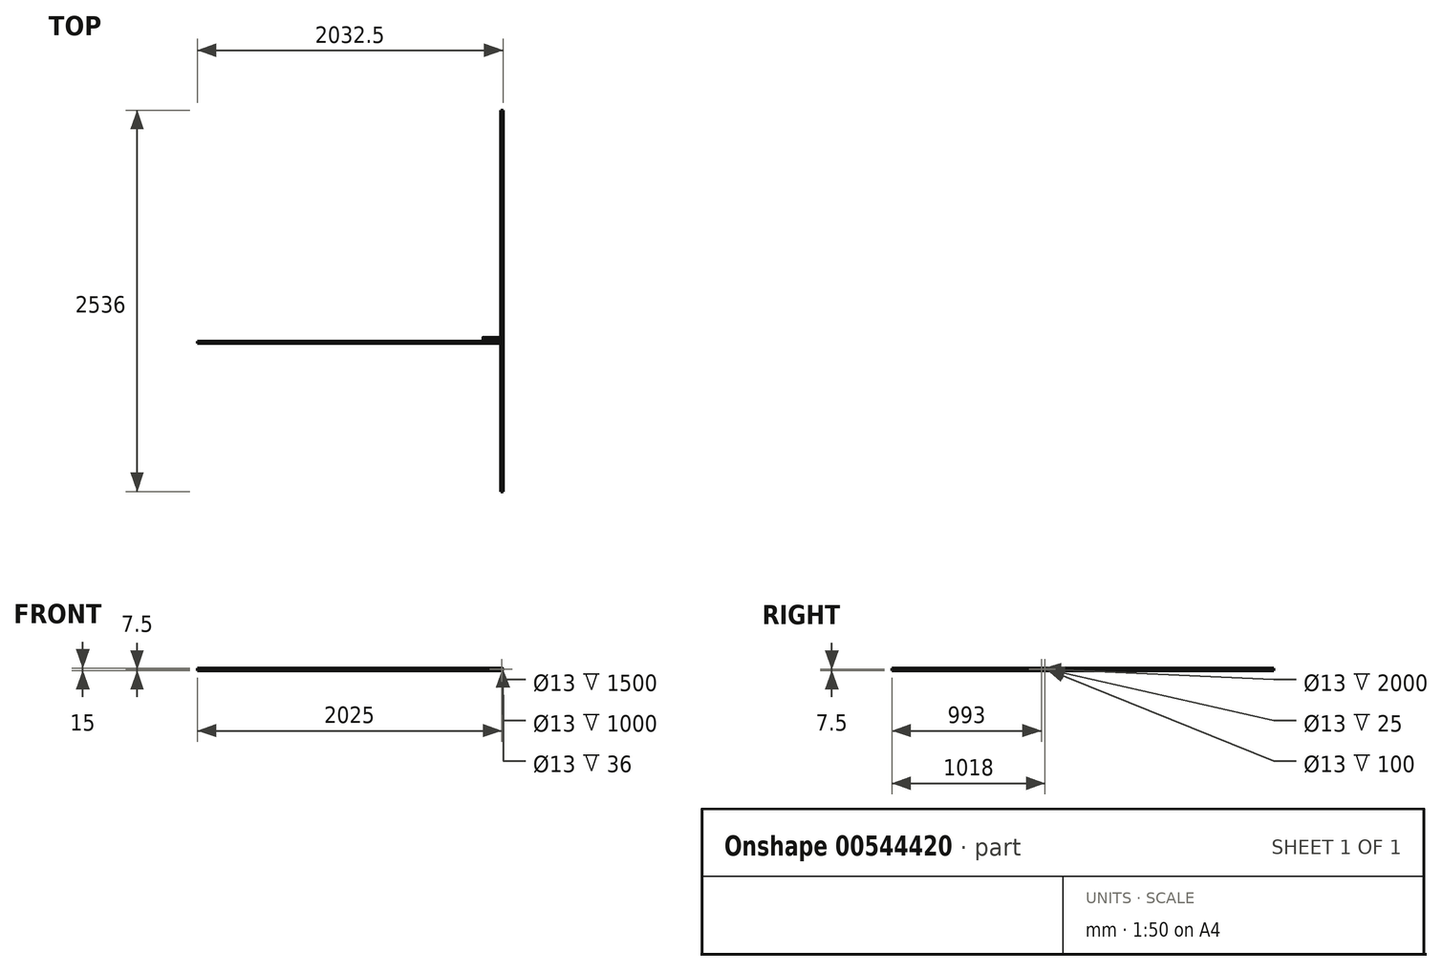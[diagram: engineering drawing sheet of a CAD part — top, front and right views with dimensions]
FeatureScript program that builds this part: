
annotation { "Feature Type Name" : "Feature", "Feature Type Description" : "" }
export const myFeature = defineFeature(function(context is Context, id is Id, definition is map)
    precondition{}
    {
        {
            var Q0;
            Q0=qCreatedBy(makeId("Front.planeOp"),FACE);
            var sketch = newSketch(context, id + "F0", { "sketchPlane" : qUnion([Q0])});
            skCircle(sketch, "E0", {"center": v(25, 0) * mm, "radius": 7.5 * mm});
            skCircle(sketch, "E1", {"center": v(25, 0) * mm, "radius": 6.5 * mm});
            skLineSegment(sketch, "E2", {"start": v(0, 0) * mm, "end": v(0, -17.9) * mm});
            skSolve(sketch);
        }
        {
            var Q0;
            Q0=makeQuery(id+"F0.imprint","IMPRINT",FACE,{"disambiguationData":[TD([[makeQuery(id+"F0.imprint","IMPRINT",EDGE,{"derivedFrom":sQuery(id+"F0.wireOp",EDGE,"E0")}),1.0]])]});
            extrude(context, id + "F1", {"entities" : qUnion([Q0]), "depth" : 18 * mm, "offsetDistance" : 25 * mm, "hasSecondDirection" : true, "secondDirectionOppositeDirection" : true, "secondDirectionDepth" : 18 * mm});
        }
        {
            var Q0;
            Q0=qCreatedBy(makeId("Right.planeOp"),FACE);
            var sketch = newSketch(context, id + "F2", { "sketchPlane" : qUnion([Q0])});
            skCircle(sketch, "E3", {"center": v(0, 0) * mm, "radius": 7.5 * mm});
            skCircle(sketch, "E4", {"center": v(0, 0) * mm, "radius": 6.5 * mm});
            skSolve(sketch);
        }
        {
            var Q0;
            Q0=makeQuery(id+"F2.imprint","IMPRINT",FACE,{"disambiguationData":[TD([[makeQuery(id+"F2.imprint","IMPRINT",EDGE,{"derivedFrom":sQuery(id+"F2.wireOp",EDGE,"E4")}),1.0]])]});
            var Q1;
            Q1=makeQuery(id+"F1.opExtrude","SWEPT_FACE",FACE,{"disambiguationData":[OSD([sQuery(id+"F0.wireOp",EDGE,"E1")])]});
            var Q2;
            Q2=makeQuery(id+"F1.opExtrude","SWEPT_BODY",BODY,{"disambiguationData":[OSD([sQuery(id+"F0.wireOp",EDGE,"E0"),sQuery(id+"F0.wireOp",EDGE,"E1")])]});
            extrude(context, id + "F3", {"entities" : qUnion([Q0]), "operationType" : NewBodyOperationType.REMOVE, "endBound" : BoundingType.UP_TO_SURFACE, "depth" : 25 * mm, "endBoundEntityFace" : qUnion([Q1]), "endBoundEntityBody" : qUnion([Q2]), "offsetDistance" : 25 * mm});
        }
        {
            var Q0;
            Q0=makeQuery(id+"F2.imprint","IMPRINT",FACE,{"disambiguationData":[TD([[makeQuery(id+"F2.imprint","IMPRINT",EDGE,{"derivedFrom":sQuery(id+"F2.wireOp",EDGE,"E3")}),1.0]])]});
            var Q1;
            Q1=makeQuery(id+"F1.opExtrude","SWEPT_BODY",BODY,{"disambiguationData":[OSD([sQuery(id+"F0.wireOp",EDGE,"E0"),sQuery(id+"F0.wireOp",EDGE,"E1")])]});
            extrude(context, id + "F4", {"entities" : qUnion([Q0]), "operationType" : NewBodyOperationType.ADD, "endBound" : BoundingType.UP_TO_BODY, "depth" : 25 * mm, "endBoundEntityBody" : qUnion([Q1]), "offsetDistance" : 25 * mm});
        }
        {
            var Q0;
            Q0=makeQuery(id+"F1.opExtrude","CAP_FACE",FACE,{"disambiguationData":[OSD([sQuery(id+"F0.wireOp",EDGE,"E0"),sQuery(id+"F0.wireOp",EDGE,"E1")])],"isStart":false});
            extrude(context, id + "F5", {"entities" : qUnion([Q0]), "depth" : 1000 * mm, "offsetDistance" : 25 * mm});
        }
        {
            var Q0;
            Q0=makeQuery(id+"F2.imprint","IMPRINT",FACE,{"disambiguationData":[TD([[makeQuery(id+"F2.imprint","IMPRINT",EDGE,{"derivedFrom":sQuery(id+"F2.wireOp",EDGE,"E3")}),1.0]])]});
            extrude(context, id + "F6", {"entities" : qUnion([Q0]), "oppositeDirection" : true, "depth" : 100 * mm, "offsetDistance" : 25 * mm});
        }
        {
            var Q0;
            Q0=makeQuery(id+"F1.opExtrude","CAP_FACE",FACE,{"disambiguationData":[OSD([sQuery(id+"F0.wireOp",EDGE,"E0"),sQuery(id+"F0.wireOp",EDGE,"E1")])],"isStart":true});
            extrude(context, id + "F7", {"entities" : qUnion([Q0]), "depth" : 1500 * mm, "offsetDistance" : 25 * mm});
        }
        {
            var Q0;
            Q0=makeQuery(id+"F0.imprint","IMPRINT",FACE,{"disambiguationData":[TD([[makeQuery(id+"F0.imprint","IMPRINT",EDGE,{"derivedFrom":sQuery(id+"F0.wireOp",EDGE,"E0")}),1.0]])]});
            var Q1;
            Q1=sQuery(id+"F0.wireOp",EDGE,"E2");
            revolve(context, id + "F8", {"entities" : qUnion([Q0]), "axis" : qUnion([Q1]), "revolveType" : RevolveType.ONE_DIRECTION, "angle" : 90 * degree});
        }
        {
            var Q0;
            Q0=makeQuery(id+"F8.opRevolve","CAP_FACE",FACE,{"disambiguationData":[OSD([sQuery(id+"F0.wireOp",EDGE,"E0"),sQuery(id+"F0.wireOp",EDGE,"E1")])],"isStart":false});
            extrude(context, id + "F9", {"entities" : qUnion([Q0]), "depth" : 2000 * mm, "offsetDistance" : 25 * mm});
        }
    });
